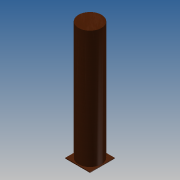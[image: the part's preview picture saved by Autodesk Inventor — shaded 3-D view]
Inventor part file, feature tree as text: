
AUTODESK INVENTOR PART (.ipt)
format: ipt  version: 2013 (Build 170138000, 138)  size: 80,896 bytes
history: native  units: in
note: dims shown in document units (in); Inventor stores cm internally (conversion verified against a paired STEP export)
features: extrude x2, sketch x2
ambient origin geometry x8: Origin, YZ Plane, XZ Plane, XY Plane, X Axis, Y Axis, Z Axis, Center Point
bodies: Solid1 (feature_tree)
feature tree (4):
  extrude  "Extrusion1"  Depth=30.0in
  extrude  "Extrusion2"  Depth=28.0in
  sketch  "Sketch1"  dims[d0=30.0in d1=30.0in]
  sketch  "Sketch2"  dims[d2=1.0in d3=0.0in d4=28.0in d6=144.0in d7=0.0in]
